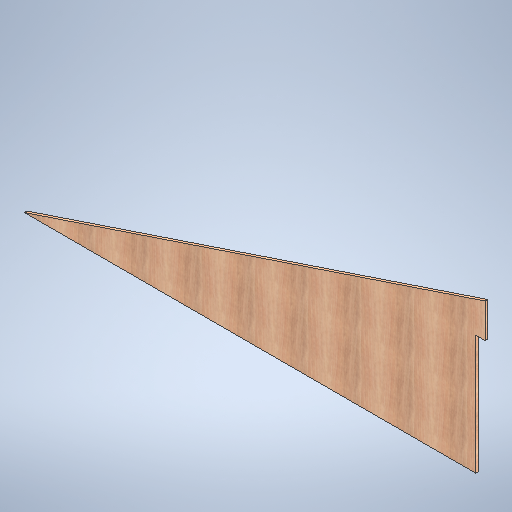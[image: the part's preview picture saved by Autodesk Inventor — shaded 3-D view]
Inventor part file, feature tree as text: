
AUTODESK INVENTOR PART (.ipt)
format: ipt  version: 2025 (Build 290162010, 162A)  size: 338,432 bytes
history: native  units: in
note: dims shown in document units (in); Inventor stores cm internally (conversion verified against a paired STEP export)
features: extrude x1, sketch x1
ambient origin geometry x8: Origin, YZ Plane, XZ Plane, XY Plane, X Axis, Y Axis, Z Axis, Center Point
bodies: Solid1 (feature_tree)
feature tree (2):
  extrude  "Extrusion1"  Depth=0.5in
  sketch  "Sketch1"  dims[d1=29.849in d3=0.5in d4=132.0in d6=5.5in d8=3.5in d9=42.875in d10=0.5in d11=0.0in d12=1.8815in d14=0.625in d16=48.0in d17=85.0in d20=2.2565in]
